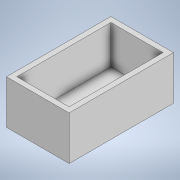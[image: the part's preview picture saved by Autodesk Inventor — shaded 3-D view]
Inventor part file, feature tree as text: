
AUTODESK INVENTOR PART (.ipt)
format: ipt  version: 2020 (Build 240168000, 168)  size: 101,888 bytes
history: native  units: in
note: dims shown in document units (in); Inventor stores cm internally (conversion verified against a paired STEP export)
features: extrude x1, shell x1, sketch x1
ambient origin geometry x8: Origin, YZ Plane, XZ Plane, XY Plane, X Axis, Y Axis, Z Axis, Center Point
bodies: Solid1 (feature_tree)
feature tree (3):
  extrude  "Extrusion1"  Depth=5.0in
  shell  "Shell1"  Thickness=2.1in
  sketch  "Sketch1"  dims[d0=3.0in d1=5.0in d2=2.1in d3=0.0in d4=0.25in]
